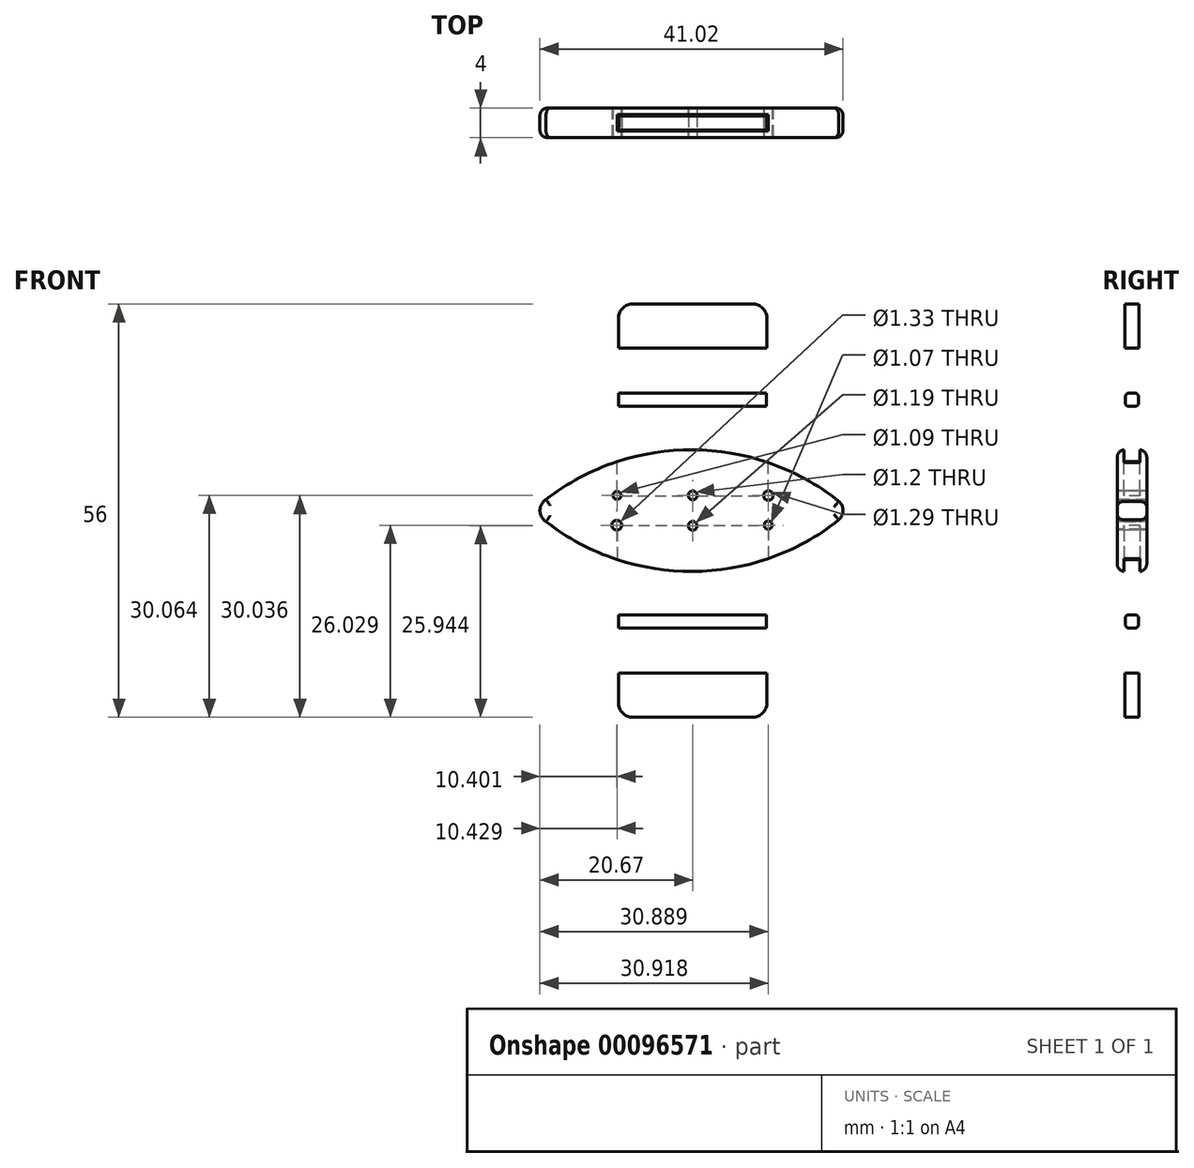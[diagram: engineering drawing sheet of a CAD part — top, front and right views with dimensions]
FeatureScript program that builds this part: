
annotation { "Feature Type Name" : "Feature", "Feature Type Description" : "" }
export const myFeature = defineFeature(function(context is Context, id is Id, definition is map)
    precondition{}
    {
        {
            var Q0;
            Q0=qCreatedBy(makeId("Front.planeOp"),FACE);
            var sketch = newSketch(context, id + "F0", { "sketchPlane" : qUnion([Q0])});
            skArc(sketch, "E0", {"start": v(19.78, 1.27) * mm, "mid": v(0, 8.24) * mm, "end": v(-19.85, 1.5) * mm});
            skArc(sketch, "E1", {"start": v(-19.85, 1.5) * mm, "mid": v(-20.45, 0.85) * mm, "end": v(-20.67, 0) * mm});
            skArc(sketch, "E2", {"start": v(20.35, 0) * mm, "mid": v(20.2, 0.7) * mm, "end": v(19.78, 1.27) * mm});
            skLineSegment(sketch, "E3", {"start": v(-20.67, 0) * mm, "end": v(20.35, 0) * mm});
            skPoint(sketch, "E4.orphan", {"position": v(-19.85, -1.5) * mm});
            skPoint(sketch, "E5.orphan", {"position": v(19.78, -1.27) * mm});
            skPoint(sketch, "E6.orphan", {"position": v(-24.92, 0) * mm});
            skSolve(sketch);
        }
        {
            var Q0;
            Q0=makeQuery(id+"F0.imprint","IMPRINT",FACE,{"disambiguationData":[TD([[makeQuery(id+"F0.imprint","IMPRINT",EDGE,{"derivedFrom":sQuery(id+"F0.wireOp",EDGE,"E0")}),1.0]])]});
            extrude(context, id + "F1", {"entities" : qUnion([Q0]), "depth" : 4 * mm, "symmetric" : true});
        }
        {
            var Q0;
            Q0=makeQuery(id+"F1.opExtrude","CAP_EDGE",EDGE,{"disambiguationData":[OSD([sQuery(id+"F0.wireOp",EDGE,"E2")])],"isStart":false});
            var Q1;
            Q1=makeQuery(id+"F1.opExtrude","CAP_EDGE",EDGE,{"disambiguationData":[OSD([sQuery(id+"F0.wireOp",EDGE,"E0")])],"isStart":false});
            var Q2;
            Q2=makeQuery(id+"F1.opExtrude","CAP_EDGE",EDGE,{"disambiguationData":[OSD([sQuery(id+"F0.wireOp",EDGE,"E1")])],"isStart":false});
            var Q3;
            Q3=makeQuery(id+"F1.opExtrude","CAP_EDGE",EDGE,{"disambiguationData":[OSD([sQuery(id+"F0.wireOp",EDGE,"a06b3a35-f8c0-4859-9cac-9e7be04928f50.MirrorCS")])],"isStart":false});
            var Q4;
            Q4=makeQuery(id+"F1.opExtrude","CAP_EDGE",EDGE,{"disambiguationData":[OSD([sQuery(id+"F0.wireOp",EDGE,"E2")])],"isStart":true});
            var Q5;
            Q5=makeQuery(id+"F1.opExtrude","CAP_EDGE",EDGE,{"disambiguationData":[OSD([sQuery(id+"F0.wireOp",EDGE,"E0")])],"isStart":true});
            var Q6;
            Q6=makeQuery(id+"F1.opExtrude","CAP_EDGE",EDGE,{"disambiguationData":[OSD([sQuery(id+"F0.wireOp",EDGE,"E1")])],"isStart":true});
            var Q7;
            Q7=makeQuery(id+"F1.opExtrude","CAP_EDGE",EDGE,{"disambiguationData":[OSD([sQuery(id+"F0.wireOp",EDGE,"a06b3a35-f8c0-4859-9cac-9e7be04928f50.MirrorCS")])],"isStart":true});
            fillet(context, id + "F2", {"entities" : qUnion([Q0, Q1, Q2, Q3, Q4, Q5, Q6, Q7]), "radius" : 1 * mm, "tangentPropagation" : true, "allowEdgeOverflow" : false});
        }
        {
            var Q0;
            Q0=qCreatedBy(makeId("Top.planeOp"),FACE);
            cPlane(context, id + "F3", {"entities" : qUnion([Q0]), "cplaneType" : CPlaneType.OFFSET, "offset" : 15 * mm, "width" : 150 * mm, "height" : 150 * mm});
        }
        {
            var Q0;
            Q0=qCreatedBy(id+"F3.planeOp",FACE);
            var sketch = newSketch(context, id + "F4", { "sketchPlane" : qUnion([Q0])});
            skLineSegment(sketch, "E7.bottom", {"start": v(-10, 0.9) * mm, "end": v(10, 0.9) * mm});
            skLineSegment(sketch, "E7.top", {"start": v(-10, -0.9) * mm, "end": v(10, -0.9) * mm});
            skLineSegment(sketch, "E7.left", {"start": v(-10, 0.9) * mm, "end": v(-10, -0.9) * mm});
            skLineSegment(sketch, "E7.right", {"start": v(10, 0.9) * mm, "end": v(10, -0.9) * mm});
            skPoint(sketch, "E7.middle", {"position": v(0, 0) * mm});
            skSolve(sketch);
        }
        {
            var Q0;
            Q0=makeQuery(id+"F4.imprint","IMPRINT",FACE,{"disambiguationData":[TD([[makeQuery(id+"F4.imprint","IMPRINT",EDGE,{"derivedFrom":sQuery(id+"F4.wireOp",EDGE,"E7.bottom")}),-1.0]])]});
            extrude(context, id + "F5", {"entities" : qUnion([Q0]), "depth" : 1.8 * mm, "symmetric" : true});
        }
        {
            var Q0;
            Q0=makeQuery(id+"F5.opExtrude","CAP_EDGE",EDGE,{"disambiguationData":[OSD([sQuery(id+"F4.wireOp",EDGE,"E7.top")])],"isStart":false});
            var Q1;
            Q1=makeQuery(id+"F5.opExtrude","CAP_EDGE",EDGE,{"disambiguationData":[OSD([sQuery(id+"F4.wireOp",EDGE,"E7.top")])],"isStart":true});
            var Q2;
            Q2=makeQuery(id+"F5.opExtrude","CAP_EDGE",EDGE,{"disambiguationData":[OSD([sQuery(id+"F4.wireOp",EDGE,"E7.bottom")])],"isStart":false});
            var Q3;
            Q3=makeQuery(id+"F5.opExtrude","CAP_EDGE",EDGE,{"disambiguationData":[OSD([sQuery(id+"F4.wireOp",EDGE,"E7.bottom")])],"isStart":true});
            fillet(context, id + "F6", {"entities" : qUnion([Q0, Q1, Q2, Q3]), "radius" : 0.5 * mm, "tangentPropagation" : true, "allowEdgeOverflow" : false});
        }
        {
            var Q0;
            Q0=qCreatedBy(makeId("Top.planeOp"),FACE);
            cPlane(context, id + "F7", {"entities" : qUnion([Q0]), "cplaneType" : CPlaneType.OFFSET, "offset" : 10 * mm, "width" : 150 * mm, "height" : 150 * mm});
        }
        {
            var Q0;
            Q0=qCreatedBy(id+"F7.planeOp",FACE);
            var sketch = newSketch(context, id + "F8", { "sketchPlane" : qUnion([Q0])});
            skLineSegment(sketch, "E8.bottom", {"start": v(-10.24, 1.1) * mm, "end": v(10.24, 1.1) * mm});
            skLineSegment(sketch, "E8.top", {"start": v(-10.24, -1.1) * mm, "end": v(10.24, -1.1) * mm});
            skLineSegment(sketch, "E8.left", {"start": v(-10.24, 1.1) * mm, "end": v(-10.24, -1.1) * mm});
            skLineSegment(sketch, "E8.right", {"start": v(10.24, 1.1) * mm, "end": v(10.24, -1.1) * mm});
            skPoint(sketch, "E8.middle", {"position": v(0, 0) * mm});
            skSolve(sketch);
        }
        {
            var Q0;
            Q0=makeQuery(id+"F8.imprint","IMPRINT",FACE,{"disambiguationData":[TD([[makeQuery(id+"F8.imprint","IMPRINT",EDGE,{"derivedFrom":sQuery(id+"F8.wireOp",EDGE,"E8.bottom")}),-1.0]])]});
            extrude(context, id + "F9", {"entities" : qUnion([Q0]), "operationType" : NewBodyOperationType.REMOVE, "oppositeDirection" : true, "depth" : 8 * mm});
        }
        {
            var Q0;
            Q0=qCreatedBy(makeId("Top.planeOp"),FACE);
            cPlane(context, id + "F10", {"entities" : qUnion([Q0]), "cplaneType" : CPlaneType.OFFSET, "offset" : 25 * mm, "width" : 150 * mm, "height" : 150 * mm});
        }
        {
            var Q0;
            Q0=qCreatedBy(id+"F10.planeOp",FACE);
            var sketch = newSketch(context, id + "F11", { "sketchPlane" : qUnion([Q0])});
            skLineSegment(sketch, "E9.bottom", {"start": v(-10.05, 0.94) * mm, "end": v(10.05, 0.94) * mm});
            skLineSegment(sketch, "E9.top", {"start": v(-10.05, -0.94) * mm, "end": v(10.05, -0.94) * mm});
            skLineSegment(sketch, "E9.left", {"start": v(-10.05, 0.94) * mm, "end": v(-10.05, -0.94) * mm});
            skLineSegment(sketch, "E9.right", {"start": v(10.05, 0.94) * mm, "end": v(10.05, -0.94) * mm});
            skPoint(sketch, "E9.middle", {"position": v(0, 0) * mm});
            skSolve(sketch);
        }
        {
            var Q0;
            Q0=makeQuery(id+"F11.imprint","IMPRINT",FACE,{"disambiguationData":[TD([[makeQuery(id+"F11.imprint","IMPRINT",EDGE,{"derivedFrom":sQuery(id+"F11.wireOp",EDGE,"E9.bottom")}),-1.0]])]});
            extrude(context, id + "F12", {"entities" : qUnion([Q0]), "depth" : 6 * mm, "symmetric" : true});
        }
        {
            var Q0;
            Q0=makeQuery(id+"F12.opExtrude","CAP_EDGE",EDGE,{"disambiguationData":[OSD([sQuery(id+"F11.wireOp",EDGE,"E9.right")])],"isStart":false});
            var Q1;
            Q1=makeQuery(id+"F12.opExtrude","CAP_EDGE",EDGE,{"disambiguationData":[OSD([sQuery(id+"F11.wireOp",EDGE,"E9.left")])],"isStart":false});
            fillet(context, id + "F13", {"entities" : qUnion([Q0, Q1]), "radius" : 2 * mm, "tangentPropagation" : true, "allowEdgeOverflow" : false});
        }
        {
            var Q0;
            Q0=makeQuery(id+"F1.opExtrude","SWEPT_BODY",BODY,{"disambiguationData":[OSD([sQuery(id+"F0.wireOp",EDGE,"E0"),sQuery(id+"F0.wireOp",EDGE,"E1"),sQuery(id+"F0.wireOp",EDGE,"E2"),sQuery(id+"F0.wireOp",EDGE,"E3")])]});
            var Q1;
            Q1=makeQuery(id+"F5.opExtrude","SWEPT_BODY",BODY,{"disambiguationData":[OSD([sQuery(id+"F4.wireOp",EDGE,"E7.bottom"),sQuery(id+"F4.wireOp",EDGE,"E7.top"),sQuery(id+"F4.wireOp",EDGE,"E7.left"),sQuery(id+"F4.wireOp",EDGE,"E7.right")])]});
            var Q2;
            Q2=makeQuery(id+"F12.opExtrude","SWEPT_BODY",BODY,{"disambiguationData":[OSD([sQuery(id+"F11.wireOp",EDGE,"E9.bottom"),sQuery(id+"F11.wireOp",EDGE,"E9.top"),sQuery(id+"F11.wireOp",EDGE,"E9.left"),sQuery(id+"F11.wireOp",EDGE,"E9.right")])]});
            var Q3;
            Q3=qCreatedBy(makeId("Top.planeOp"),FACE);
            mirror(context, id + "F14", {"operationType" : NewBodyOperationType.ADD, "entities" : qUnion([Q0, Q1, Q2]), "mirrorPlane" : qUnion([Q3])});
        }
        {
            var Q0;
            Q0=qCreatedBy(makeId("Front.planeOp"),FACE);
            cPlane(context, id + "F15", {"entities" : qUnion([Q0]), "cplaneType" : CPlaneType.OFFSET, "offset" : 10 * mm, "width" : 150 * mm, "height" : 150 * mm});
        }
        {
            var Q0;
            Q0=qCreatedBy(id+"F15.planeOp",FACE);
            var sketch = newSketch(context, id + "F16", { "sketchPlane" : qUnion([Q0])});
            skCircle(sketch, "E10", {"center": v(-10.24, 2.06) * mm, "radius": 0.54 * mm});
            skCircle(sketch, "E11", {"center": v(10.25, 2.04) * mm, "radius": 0.64 * mm});
            skCircle(sketch, "E12", {"center": v(-10.27, -1.97) * mm, "radius": 0.66 * mm});
            skCircle(sketch, "E13", {"center": v(10.22, -1.97) * mm, "radius": 0.54 * mm});
            skCircle(sketch, "E14", {"center": v(0, -2.06) * mm, "radius": 0.6 * mm});
            skCircle(sketch, "E15", {"center": v(0, 2.06) * mm, "radius": 0.6 * mm});
            skSolve(sketch);
        }
        {
            var Q0;
            Q0 = qSketchRegion(id + "F16", true);
            extrude(context, id + "F17", {"entities" : qUnion([Q0]), "operationType" : NewBodyOperationType.REMOVE, "oppositeDirection" : true, "depth" : 25 * mm});
        }
    });
